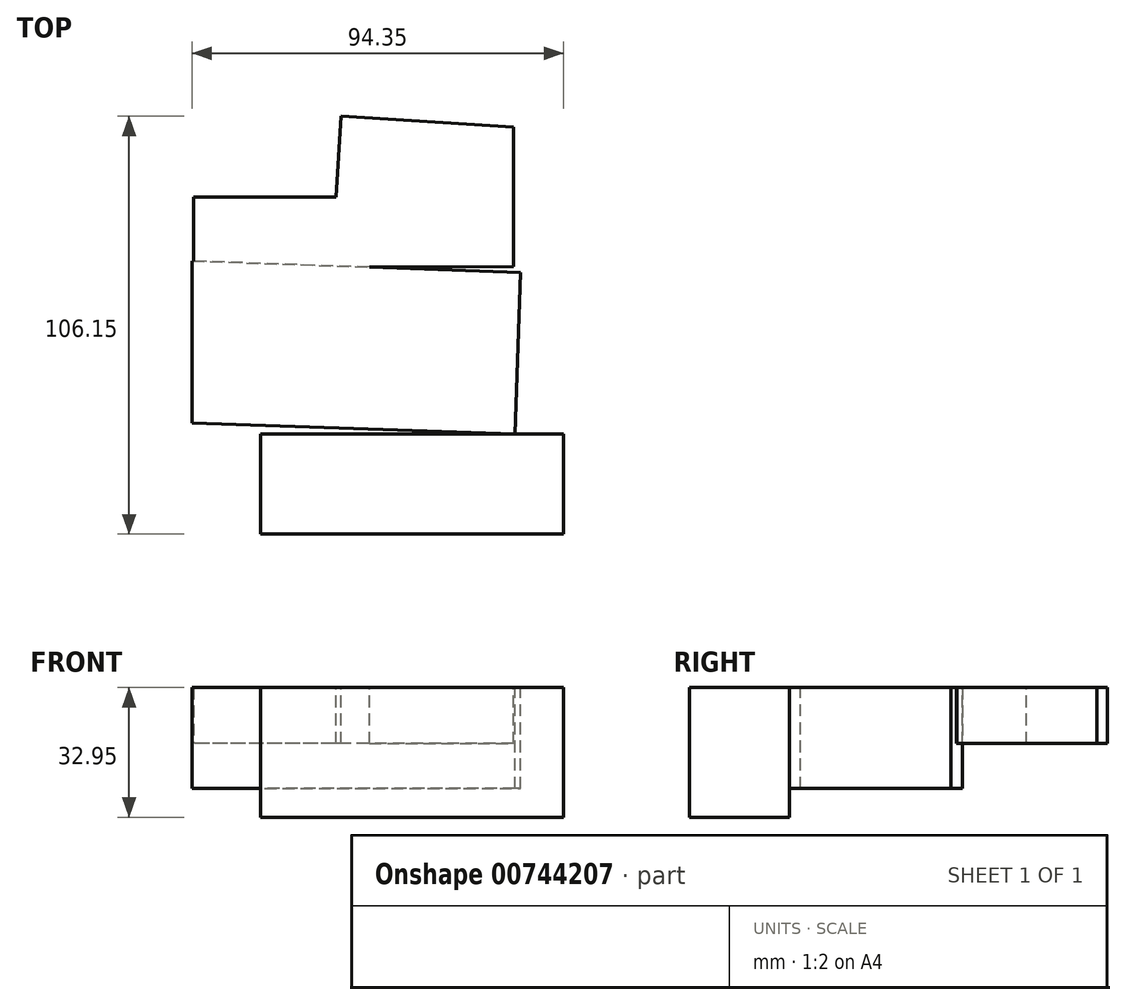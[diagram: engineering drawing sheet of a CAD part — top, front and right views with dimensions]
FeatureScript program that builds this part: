
annotation { "Feature Type Name" : "Feature", "Feature Type Description" : "" }
export const myFeature = defineFeature(function(context is Context, id is Id, definition is map)
    precondition{}
    {
        {
            var Q0;
            Q0=qCreatedBy(makeId("Front.planeOp"),FACE);
            var sketch = newSketch(context, id + "F0", { "sketchPlane" : qUnion([Q0])});
            skLineSegment(sketch, "E0", {"start": v(0, 0) * mm, "end": v(0, -32.95) * mm});
            skLineSegment(sketch, "E1", {"start": v(0, -32.95) * mm, "end": v(76.99, -32.95) * mm});
            skLineSegment(sketch, "E2", {"start": v(76.99, -32.95) * mm, "end": v(76.99, 0) * mm});
            skLineSegment(sketch, "E3", {"start": v(76.99, 0) * mm, "end": v(0, 0) * mm});
            skSolve(sketch);
        }
        {
            var Q0;
            Q0=makeQuery(id+"F0.imprint","IMPRINT",FACE,{"disambiguationData":[TD([[makeQuery(id+"F0.imprint","IMPRINT",EDGE,{"derivedFrom":sQuery(id+"F0.wireOp",EDGE,"E0")}),1.0]])]});
            extrude(context, id + "F1", {"entities" : qUnion([Q0]), "depth" : 25.4 * mm, "offsetDistance" : 25.4 * mm});
        }
        {
            var Q0;
            Q0=qCreatedBy(makeId("Top.planeOp"),FACE);
            var sketch = newSketch(context, id + "F2", { "sketchPlane" : qUnion([Q0])});
            skLineSegment(sketch, "E4", {"start": v(-17.36, 12.95) * mm, "end": v(-17.36, 43.97) * mm});
            skLineSegment(sketch, "E5", {"start": v(-17.36, 43.97) * mm, "end": v(66.08, 41.07) * mm});
            skLineSegment(sketch, "E6", {"start": v(66.08, 41.07) * mm, "end": v(64.66, 0) * mm});
            skLineSegment(sketch, "E7", {"start": v(64.66, 0) * mm, "end": v(-17.36, 2.85) * mm});
            skLineSegment(sketch, "E8", {"start": v(-17.36, 2.85) * mm, "end": v(-17.36, 12.95) * mm});
            skSolve(sketch);
        }
        {
            var Q0;
            Q0=makeQuery(id+"F2.imprint","IMPRINT",FACE,{"disambiguationData":[TD([[makeQuery(id+"F2.imprint","IMPRINT",EDGE,{"derivedFrom":sQuery(id+"F2.wireOp",EDGE,"E4")}),-1.0]])]});
            extrude(context, id + "F3", {"entities" : qUnion([Q0]), "oppositeDirection" : true, "depth" : 25.65 * mm, "offsetDistance" : 25.4 * mm});
        }
        {
            var Q0;
            Q0=qCreatedBy(makeId("Top.planeOp"),FACE);
            var sketch = newSketch(context, id + "F4", { "sketchPlane" : qUnion([Q0])});
            skLineSegment(sketch, "E9", {"start": v(64.26, 42.56) * mm, "end": v(64.26, 78.06) * mm});
            skLineSegment(sketch, "E10", {"start": v(64.26, 78.06) * mm, "end": v(20.51, 80.75) * mm});
            skLineSegment(sketch, "E11", {"start": v(20.51, 80.75) * mm, "end": v(19.25, 60.24) * mm});
            skLineSegment(sketch, "E12", {"start": v(19.25, 60.24) * mm, "end": v(-17, 60.24) * mm});
            skLineSegment(sketch, "E13", {"start": v(-17, 60.24) * mm, "end": v(-17, 42.2) * mm});
            skLineSegment(sketch, "E14", {"start": v(-17, 42.2) * mm, "end": v(64.26, 42.56) * mm});
            skSolve(sketch);
        }
        {
            var Q0;
            Q0=makeQuery(id+"F4.imprint","IMPRINT",FACE,{"disambiguationData":[TD([[makeQuery(id+"F4.imprint","IMPRINT",EDGE,{"derivedFrom":sQuery(id+"F4.wireOp",EDGE,"E9")}),1.0]])]});
            extrude(context, id + "F5", {"entities" : qUnion([Q0]), "operationType" : NewBodyOperationType.ADD, "oppositeDirection" : true, "depth" : 14.22 * mm, "offsetDistance" : 25.4 * mm});
        }
    });
